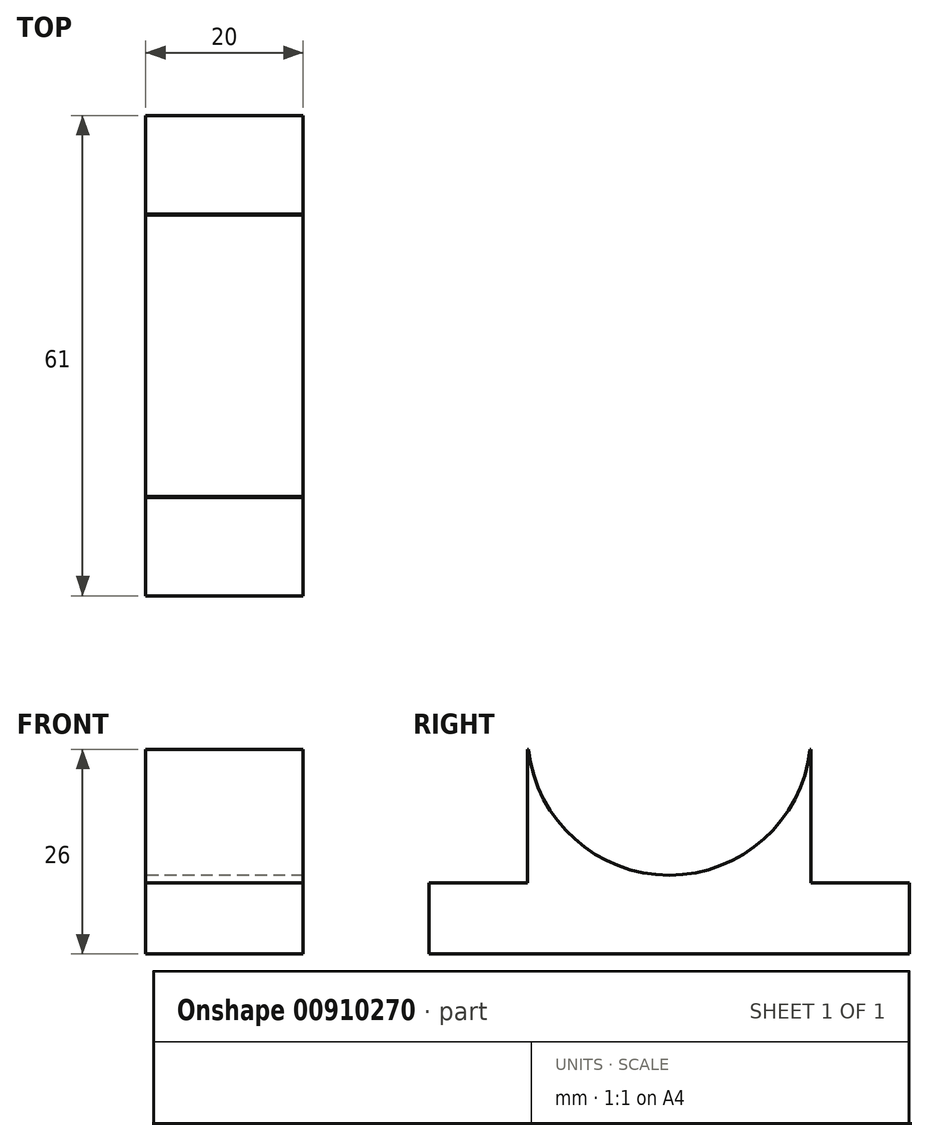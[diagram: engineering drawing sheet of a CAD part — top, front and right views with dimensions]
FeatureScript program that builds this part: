
annotation { "Feature Type Name" : "Feature", "Feature Type Description" : "" }
export const myFeature = defineFeature(function(context is Context, id is Id, definition is map)
    precondition{}
    {
        {
            var Q0;
            Q0=qCreatedBy(makeId("Right.planeOp"),FACE);
            var sketch = newSketch(context, id + "F0", { "sketchPlane" : qUnion([Q0])});
            skCircle(sketch, "E0", {"center": v(0, 0) * mm, "radius": 18 * mm});
            skCircle(sketch, "E1", {"center": v(0, 0) * mm, "radius": 23 * mm});
            skLineSegment(sketch, "E2.bottom", {"start": v(-30.5, -10) * mm, "end": v(30.5, -10) * mm});
            skLineSegment(sketch, "E2.top", {"start": v(-30.5, 10) * mm, "end": v(30.5, 10) * mm});
            skLineSegment(sketch, "E2.left", {"start": v(-30.5, -10) * mm, "end": v(-30.5, 10) * mm});
            skLineSegment(sketch, "E2.right", {"start": v(30.5, -10) * mm, "end": v(30.5, 10) * mm});
            skLineSegment(sketch, "E3", {"start": v(-30.5, 0) * mm, "end": v(30.5, 0) * mm});
            skLineSegment(sketch, "E4", {"start": v(0, 0) * mm, "end": v(0, -18) * mm});
            skPoint(sketch, "E4.endSnap0", {"position": v(0, -10) * mm});
            skLineSegment(sketch, "E5", {"start": v(0, -18) * mm, "end": v(30.5, -18) * mm});
            skLineSegment(sketch, "E6", {"start": v(0, -18) * mm, "end": v(-30.5, -18) * mm});
            skLineSegment(sketch, "E7", {"start": v(18, 0) * mm, "end": v(18.5, 0) * mm});
            skLineSegment(sketch, "E8", {"start": v(18.5, 0) * mm, "end": v(18.5, -18) * mm});
            skLineSegment(sketch, "E9", {"start": v(18.5, -18) * mm, "end": v(19.5, -18) * mm});
            skLineSegment(sketch, "E10", {"start": v(18.5, 0) * mm, "end": v(19.5, -18) * mm});
            skLineSegment(sketch, "E11", {"start": v(30.5, 0) * mm, "end": v(30.5, -18) * mm});
            skLineSegment(sketch, "E12", {"start": v(30.5, -18) * mm, "end": v(30.5, -10.5) * mm});
            skLineSegment(sketch, "E13", {"start": v(30.5, -10.5) * mm, "end": v(18.5, -10.5) * mm});
            skLineSegment(sketch, "E14", {"start": v(23, 0) * mm, "end": v(23, -10.5) * mm});
            skLineSegment(sketch, "E15", {"start": v(23, -10.5) * mm, "end": v(25, -10.5) * mm});
            skLineSegment(sketch, "E16", {"start": v(23, 0) * mm, "end": v(25, -10.5) * mm});
            skPoint(sketch, "E17.end.orphan", {"position": v(25, -18) * mm});
            skLineSegment(sketch, "E18.MirrorCS", {"start": v(-23, 0) * mm, "end": v(-25, -10.5) * mm});
            skLineSegment(sketch, "E19.MirrorCS", {"start": v(-30.5, -10.5) * mm, "end": v(-18.5, -10.5) * mm});
            skLineSegment(sketch, "E20.MirrorCS", {"start": v(-30.5, 0) * mm, "end": v(-30.5, -18) * mm});
            skLineSegment(sketch, "E21.MirrorCS", {"start": v(-18.5, 0) * mm, "end": v(-19.5, -18) * mm});
            skLineSegment(sketch, "E22.MirrorCS", {"start": v(-18, 0) * mm, "end": v(-18.5, 0) * mm});
            skLineSegment(sketch, "E23", {"start": v(-30.5, -18) * mm, "end": v(-30.5, -28) * mm});
            skLineSegment(sketch, "E24", {"start": v(-30.5, -28) * mm, "end": v(30.5, -28) * mm});
            skLineSegment(sketch, "E25", {"start": v(30.5, -18) * mm, "end": v(30.5, -28) * mm});
            skLineSegment(sketch, "E26", {"start": v(-18, 0) * mm, "end": v(-18, -18) * mm});
            skLineSegment(sketch, "E27", {"start": v(18, 0) * mm, "end": v(18, -18) * mm});
            skLineSegment(sketch, "E28", {"start": v(18, -18) * mm, "end": v(18, -19) * mm});
            skLineSegment(sketch, "E29", {"start": v(-18, -18) * mm, "end": v(-17, -18) * mm});
            skLineSegment(sketch, "E30", {"start": v(-17, -18) * mm, "end": v(-17, -19) * mm});
            skLineSegment(sketch, "E31", {"start": v(-18, -18) * mm, "end": v(-18, -19) * mm});
            skLineSegment(sketch, "E32", {"start": v(-18, -19) * mm, "end": v(-30.5, -19) * mm});
            skLineSegment(sketch, "E33", {"start": v(18, -19) * mm, "end": v(30.5, -19) * mm});
            skLineSegment(sketch, "E34", {"start": v(18, 0) * mm, "end": v(18, -1.6) * mm});
            skLineSegment(sketch, "E35", {"start": v(18, 0) * mm, "end": v(18, -2) * mm});
            skLineSegment(sketch, "E36", {"start": v(18, -2) * mm, "end": v(17.86, -2) * mm});
            skLineSegment(sketch, "E37", {"start": v(-18, 0) * mm, "end": v(-18, -2) * mm});
            skLineSegment(sketch, "E38", {"start": v(-18, -2) * mm, "end": v(-17.66, -2) * mm});
            skSolve(sketch);
        }
        {
            var Q0;
            {var subQ0=sQuery(id+"F0.wireOp",EDGE,"E2.bottom");var subQ1=sQuery(id+"F0.wireOp",EDGE,"E0");var subQ2=makeQuery(id+"F0.imprint","INTERSECT",VERTEX,{"disambiguationData":[OD(0.0)],"derivedFrom":[subQ1,subQ0]});Q0=makeQuery(id+"F0.imprint","IMPRINT",FACE,{"disambiguationData":[TD([[makeQuery(id+"F0.imprint","IMPRINT",EDGE,{"disambiguationData":[TD([[subQ2,1.0]])],"derivedFrom":subQ1}),-1.0]])]});}
            var Q1;
            {var subQ0=sQuery(id+"F0.wireOp",EDGE,"E36");var subQ1=sQuery(id+"F0.wireOp",EDGE,"E0");var subQ2=makeQuery(id+"F0.imprint","INTERSECT",VERTEX,{"derivedFrom":[subQ1,subQ0]});Q1=makeQuery(id+"F0.imprint","IMPRINT",FACE,{"disambiguationData":[TD([[makeQuery(id+"F0.imprint","IMPRINT",EDGE,{"disambiguationData":[TD([[subQ2,1.0]])],"derivedFrom":subQ1}),-1.0]])]});}
            var Q2;
            {var subQ3=sQuery(id+"F0.wireOp",EDGE,"E1");var subQ5=sQuery(id+"F0.wireOp",EDGE,"E27");var subQ6=makeQuery(id+"F0.imprint","INTERSECT",VERTEX,{"derivedFrom":[subQ3,subQ5]});Q2=makeQuery(id+"F0.imprint","IMPRINT",FACE,{"disambiguationData":[TD([[makeQuery(id+"F0.imprint","IMPRINT",EDGE,{"disambiguationData":[TD([[subQ6,1.0]])],"derivedFrom":subQ3}),1.0]])]});}
            var Q3;
            {var subQ0=sQuery(id+"F0.wireOp",EDGE,"E27");var subQ1=sQuery(id+"F0.wireOp",EDGE,"E1");var subQ2=makeQuery(id+"F0.imprint","INTERSECT",VERTEX,{"derivedFrom":[subQ1,subQ0]});Q3=makeQuery(id+"F0.imprint","IMPRINT",FACE,{"disambiguationData":[TD([[makeQuery(id+"F0.imprint","IMPRINT",EDGE,{"disambiguationData":[TD([[subQ2,1.0]])],"derivedFrom":subQ1}),-1.0]])]});}
            var Q4;
            {var subQ6=sQuery(id+"F0.wireOp",EDGE,"E24");Q4=makeQuery(id+"F0.imprint","IMPRINT",FACE,{"disambiguationData":[TD([[makeQuery(id+"F0.imprint","IMPRINT",EDGE,{"derivedFrom":subQ6}),1.0]])]});}
            var Q5;
            {var subQ3=sQuery(id+"F0.wireOp",EDGE,"E26");var subQ7=sQuery(id+"F0.wireOp",EDGE,"E1");var subQ9=makeQuery(id+"F0.imprint","INTERSECT",VERTEX,{"derivedFrom":[subQ7,subQ3]});Q5=makeQuery(id+"F0.imprint","IMPRINT",FACE,{"disambiguationData":[TD([[makeQuery(id+"F0.imprint","IMPRINT",EDGE,{"disambiguationData":[TD([[subQ9,-1.0]])],"derivedFrom":subQ7}),1.0]])]});}
            var Q6;
            {var subQ0=sQuery(id+"F0.wireOp",EDGE,"E5");var subQ1=sQuery(id+"F0.wireOp",EDGE,"E1");var subQ2=makeQuery(id+"F0.imprint","INTERSECT",VERTEX,{"derivedFrom":[subQ1,subQ0]});Q6=makeQuery(id+"F0.imprint","IMPRINT",FACE,{"disambiguationData":[TD([[makeQuery(id+"F0.imprint","IMPRINT",EDGE,{"disambiguationData":[TD([[subQ2,1.0]])],"derivedFrom":subQ1}),1.0]])]});}
            var Q7;
            {var subQ3=sQuery(id+"F0.wireOp",EDGE,"E6");var subQ5=makeQuery(id+"F0.imprint","IMPRINT",VERTEX,{"derivedFrom":subQ3});Q7=makeQuery(id+"F0.imprint","IMPRINT",FACE,{"disambiguationData":[TD([[makeQuery(id+"F0.imprint","IMPRINT",EDGE,{"disambiguationData":[TD([[subQ5,1.0]])],"derivedFrom":subQ3}),-1.0]])]});}
            extrude(context, id + "F1", {"entities" : qUnion([Q0, Q1, Q2, Q3, Q4, Q5, Q6, Q7]), "depth" : 20 * mm, "offsetDistance" : 25 * mm});
        }
    });
